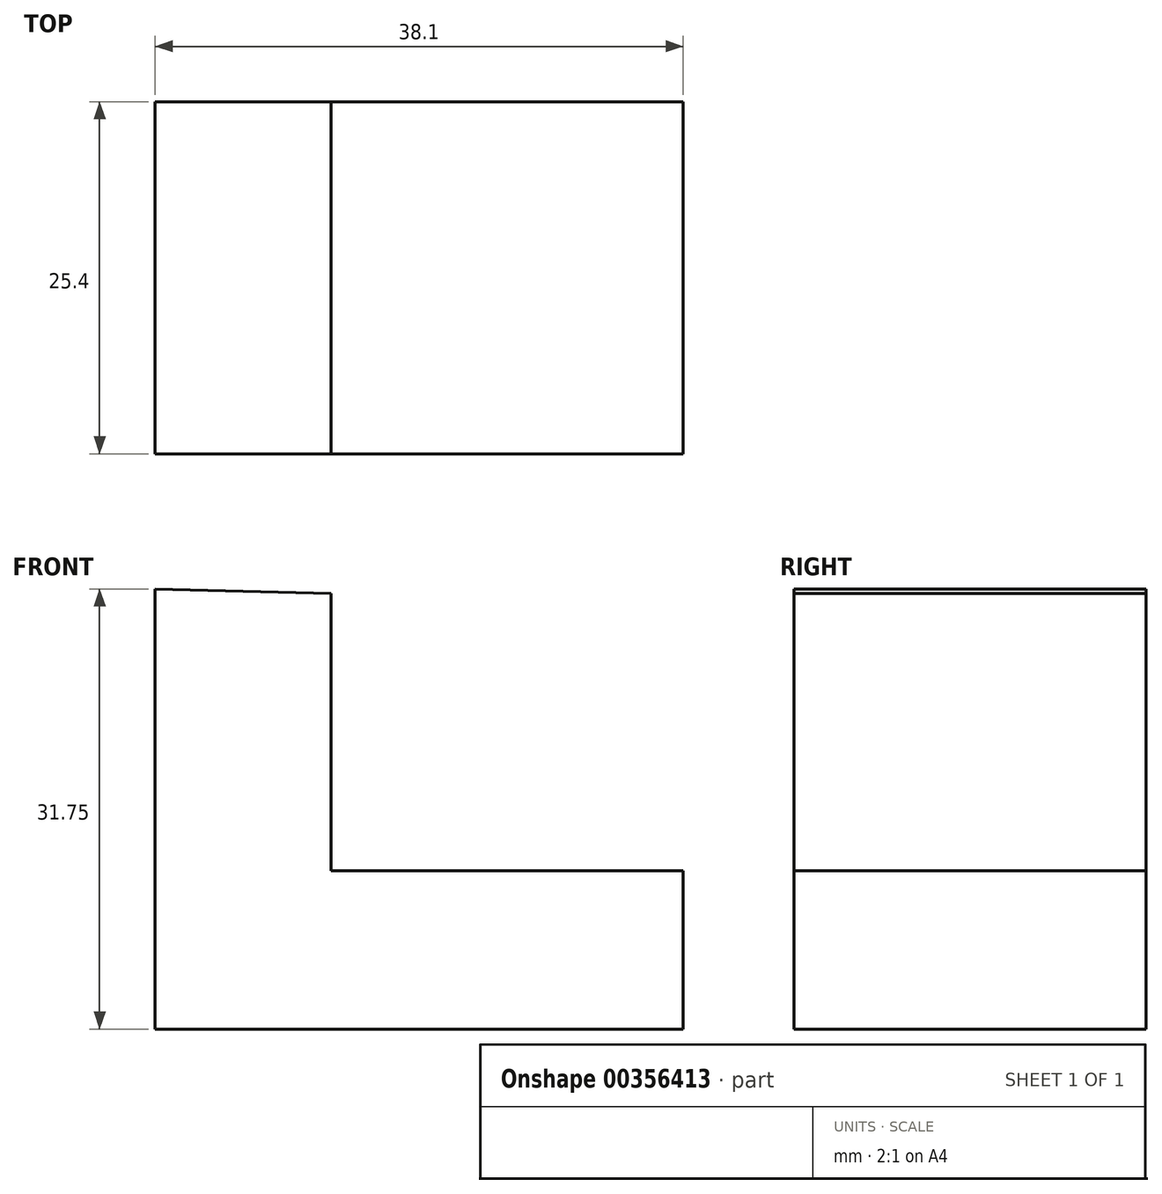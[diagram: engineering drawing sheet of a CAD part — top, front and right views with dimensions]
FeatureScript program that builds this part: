
annotation { "Feature Type Name" : "Feature", "Feature Type Description" : "" }
export const myFeature = defineFeature(function(context is Context, id is Id, definition is map)
    precondition{}
    {
        {
            var Q0;
            Q0=qCreatedBy(makeId("Front.planeOp"),FACE);
            var sketch = newSketch(context, id + "F0", { "sketchPlane" : qUnion([Q0])});
            skLineSegment(sketch, "E0", {"start": v(0, 31.75) * mm, "end": v(0, 0) * mm});
            skLineSegment(sketch, "E1", {"start": v(0, 0) * mm, "end": v(38.1, 0) * mm});
            skLineSegment(sketch, "E2", {"start": v(38.1, 0) * mm, "end": v(38.1, 11.4) * mm});
            skLineSegment(sketch, "E3", {"start": v(38.1, 11.4) * mm, "end": v(12.7, 11.4) * mm});
            skLineSegment(sketch, "E4", {"start": v(12.7, 11.4) * mm, "end": v(12.7, 31.43) * mm});
            skLineSegment(sketch, "E5", {"start": v(12.7, 31.43) * mm, "end": v(0, 31.75) * mm});
            skSolve(sketch);
        }
        {
            var Q0;
            Q0=makeQuery(id+"F0.imprint","IMPRINT",FACE,{"disambiguationData":[TD([[makeQuery(id+"F0.imprint","IMPRINT",EDGE,{"derivedFrom":sQuery(id+"F0.wireOp",EDGE,"E0")}),1.0]])]});
            extrude(context, id + "F1", {"entities" : qUnion([Q0]), "depth" : 25.4 * mm});
        }
    });
